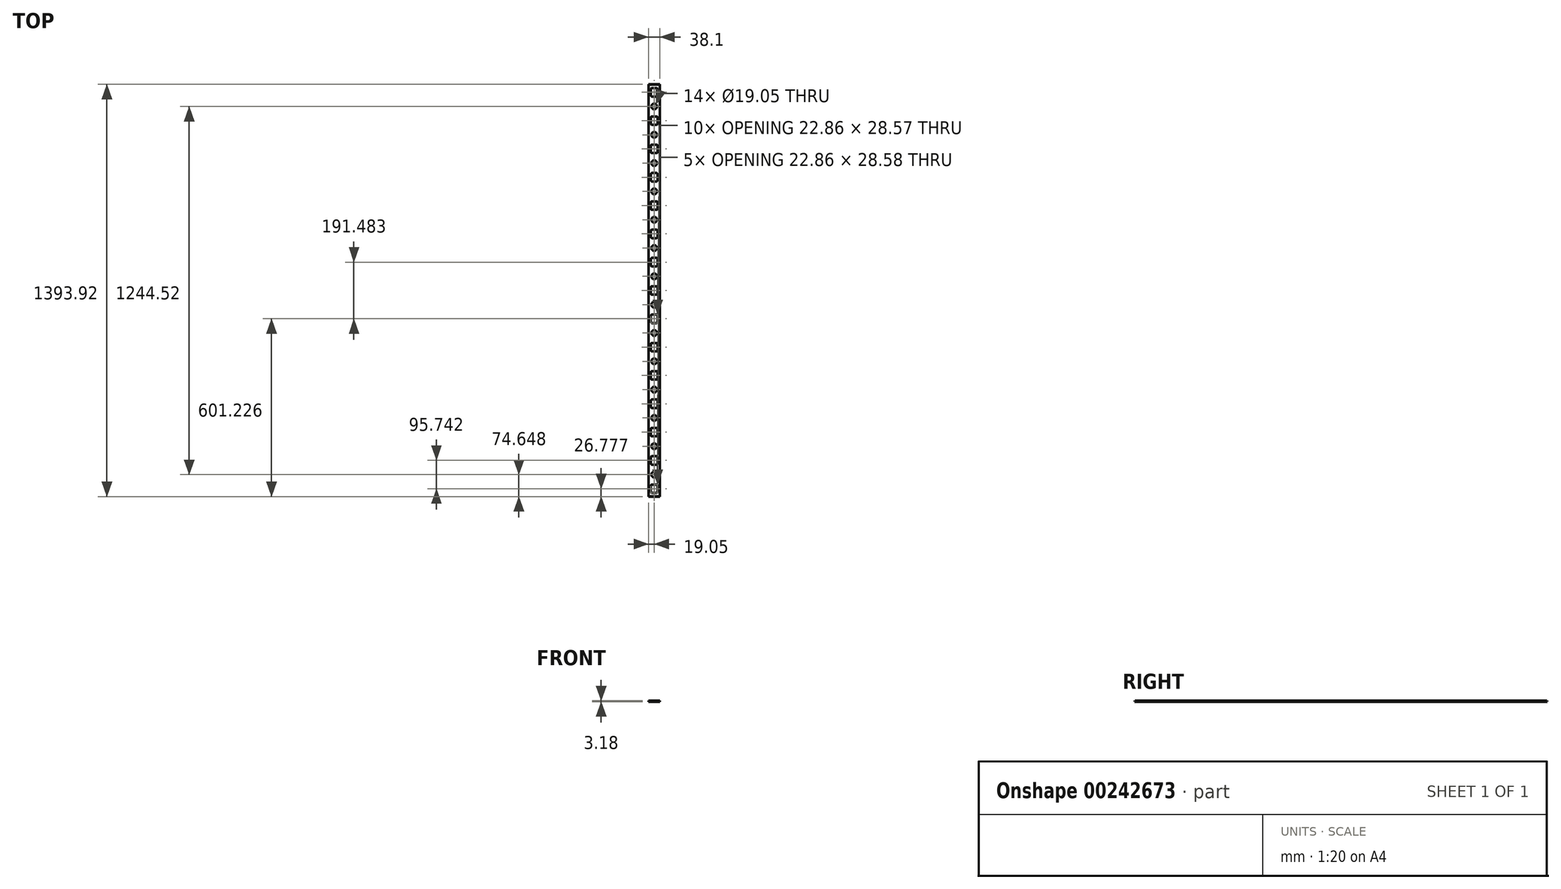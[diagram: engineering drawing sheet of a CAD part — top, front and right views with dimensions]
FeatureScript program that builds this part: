
annotation { "Feature Type Name" : "Feature", "Feature Type Description" : "" }
export const myFeature = defineFeature(function(context is Context, id is Id, definition is map)
    precondition{}
    {
        {
            var Q0;
            Q0=qCreatedBy(makeId("Front.planeOp"),FACE);
            var sketch = newSketch(context, id + "F0", { "sketchPlane" : qUnion([Q0])});
            skLineSegment(sketch, "E0.bottom", {"start": v(19.05, -1.59) * mm, "end": v(-19.05, -1.59) * mm});
            skLineSegment(sketch, "E0.top", {"start": v(19.05, 1.59) * mm, "end": v(-19.05, 1.59) * mm});
            skLineSegment(sketch, "E0.left", {"start": v(19.05, -1.59) * mm, "end": v(19.05, 1.59) * mm});
            skLineSegment(sketch, "E0.right", {"start": v(-19.05, -1.59) * mm, "end": v(-19.05, 1.59) * mm});
            skPoint(sketch, "E0.middle", {"position": v(0, 0) * mm});
            skSolve(sketch);
        }
        {
            var Q0;
            Q0 = qSketchRegion(id + "F0", true);
            extrude(context, id + "F1", {"entities" : qUnion([Q0]), "depth" : 696.96 * mm, "hasSecondDirection" : true, "secondDirectionOppositeDirection" : true, "secondDirectionDepth" : 696.96 * mm});
        }
        {
            var Q0;
            Q0=makeQuery(id+"F1.opExtrude","SWEPT_FACE",FACE,{"disambiguationData":[OSD([sQuery(id+"F0.wireOp",EDGE,"E0.left")])]});
            var sketch = newSketch(context, id + "F2", { "sketchPlane" : qUnion([Q0])});
            skLineSegment(sketch, "E1", {"start": v(-696.96, -1.59) * mm, "end": v(-696.96, 1.59) * mm});
            skLineSegment(sketch, "E2", {"start": v(-696.96, -1.59) * mm, "end": v(-695.58, 1.59) * mm});
            skLineSegment(sketch, "E3", {"start": v(-695.58, 1.59) * mm, "end": v(-696.96, 1.59) * mm});
            skLineSegment(sketch, "E4", {"start": v(0, 0) * mm, "end": v(0, -127.2) * mm, "construction": true});
            skLineSegment(sketch, "E5.MirrorCS", {"start": v(696.96, -1.59) * mm, "end": v(695.58, 1.59) * mm});
            skLineSegment(sketch, "E6.MirrorCS", {"start": v(696.96, -1.59) * mm, "end": v(696.96, 1.59) * mm});
            skLineSegment(sketch, "E7.MirrorCS", {"start": v(695.58, 1.59) * mm, "end": v(696.96, 1.59) * mm});
            skSolve(sketch);
        }
        {
            var Q0;
            Q0 = qSketchRegion(id + "F2", true);
            var Q1;
            Q1=makeQuery(id+"F1.opExtrude","SWEPT_FACE",FACE,{"disambiguationData":[OSD([sQuery(id+"F0.wireOp",EDGE,"E0.right")])]});
            extrude(context, id + "F3", {"entities" : qUnion([Q0]), "operationType" : NewBodyOperationType.REMOVE, "endBound" : BoundingType.UP_TO_SURFACE, "oppositeDirection" : true, "endBoundEntityFace" : qUnion([Q1]), "depth" : 25.4 * mm});
        }
        {
            var Q0;
            Q0=makeQuery(id+"F1.opExtrude","SWEPT_FACE",FACE,{"disambiguationData":[OSD([sQuery(id+"F0.wireOp",EDGE,"E0.top")])]});
            var sketch = newSketch(context, id + "F4", { "sketchPlane" : qUnion([Q0])});
            skLineSegment(sketch, "E8.bottom", {"start": v(7.62, -684.47) * mm, "end": v(-7.62, -684.47) * mm});
            skLineSegment(sketch, "E8.top", {"start": v(7.62, -655.9) * mm, "end": v(-7.62, -655.9) * mm});
            skLineSegment(sketch, "E8.left", {"start": v(11.43, -680.66) * mm, "end": v(11.43, -659.7) * mm});
            skLineSegment(sketch, "E8.right", {"start": v(-11.43, -680.66) * mm, "end": v(-11.43, -659.7) * mm});
            skPoint(sketch, "E8.middle", {"position": v(0, -670.18) * mm});
            skPoint(sketch, "E9.visualSharp", {"position": v(11.43, -655.9) * mm});
            skArc(sketch, "E9.filletArc", {"start": v(11.43, -659.7) * mm, "mid": v(10.31, -657.01) * mm, "end": v(7.62, -655.9) * mm});
            skPoint(sketch, "E10.visualSharp", {"position": v(-11.43, -655.9) * mm});
            skArc(sketch, "E10.filletArc", {"start": v(-7.62, -655.9) * mm, "mid": v(-10.31, -657.01) * mm, "end": v(-11.43, -659.7) * mm});
            skPoint(sketch, "E11.visualSharp", {"position": v(-11.43, -684.47) * mm});
            skArc(sketch, "E11.filletArc", {"start": v(-11.43, -680.66) * mm, "mid": v(-10.31, -683.35) * mm, "end": v(-7.62, -684.47) * mm});
            skPoint(sketch, "E12.visualSharp", {"position": v(11.43, -684.47) * mm});
            skArc(sketch, "E12.filletArc", {"start": v(7.62, -684.47) * mm, "mid": v(10.31, -683.35) * mm, "end": v(11.43, -680.66) * mm});
            skArc(sketch, "E13.0.1.0", {"start": v(7.62, -588.73) * mm, "mid": v(10.31, -587.61) * mm, "end": v(11.43, -584.92) * mm});
            skArc(sketch, "E13.0.1.1", {"start": v(11.43, -563.96) * mm, "mid": v(10.31, -561.27) * mm, "end": v(7.62, -560.15) * mm});
            skLineSegment(sketch, "E13.0.1.2", {"start": v(7.62, -560.15) * mm, "end": v(-7.62, -560.15) * mm});
            skLineSegment(sketch, "E13.0.1.3", {"start": v(-11.43, -584.92) * mm, "end": v(-11.43, -563.96) * mm});
            skArc(sketch, "E13.0.1.4", {"start": v(-11.43, -584.92) * mm, "mid": v(-10.31, -587.61) * mm, "end": v(-7.62, -588.73) * mm});
            skLineSegment(sketch, "E13.0.1.5", {"start": v(7.62, -588.73) * mm, "end": v(-7.62, -588.73) * mm});
            skLineSegment(sketch, "E13.0.1.6", {"start": v(11.43, -584.92) * mm, "end": v(11.43, -563.96) * mm});
            skArc(sketch, "E13.0.1.7", {"start": v(-7.62, -560.15) * mm, "mid": v(-10.31, -561.27) * mm, "end": v(-11.43, -563.96) * mm});
            skArc(sketch, "E13.0.2.0", {"start": v(7.62, -492.99) * mm, "mid": v(10.31, -491.87) * mm, "end": v(11.43, -489.18) * mm});
            skArc(sketch, "E13.0.2.1", {"start": v(11.43, -468.22) * mm, "mid": v(10.31, -465.53) * mm, "end": v(7.62, -464.41) * mm});
            skLineSegment(sketch, "E13.0.2.2", {"start": v(7.62, -464.41) * mm, "end": v(-7.62, -464.41) * mm});
            skLineSegment(sketch, "E13.0.2.3", {"start": v(-11.43, -489.18) * mm, "end": v(-11.43, -468.22) * mm});
            skArc(sketch, "E13.0.2.4", {"start": v(-11.43, -489.18) * mm, "mid": v(-10.31, -491.87) * mm, "end": v(-7.62, -492.99) * mm});
            skLineSegment(sketch, "E13.0.2.5", {"start": v(7.62, -492.99) * mm, "end": v(-7.62, -492.99) * mm});
            skLineSegment(sketch, "E13.0.2.6", {"start": v(11.43, -489.18) * mm, "end": v(11.43, -468.22) * mm});
            skArc(sketch, "E13.0.2.7", {"start": v(-7.62, -464.41) * mm, "mid": v(-10.31, -465.53) * mm, "end": v(-11.43, -468.22) * mm});
            skArc(sketch, "E13.0.3.0", {"start": v(7.62, -397.25) * mm, "mid": v(10.31, -396.13) * mm, "end": v(11.43, -393.44) * mm});
            skArc(sketch, "E13.0.3.1", {"start": v(11.43, -372.48) * mm, "mid": v(10.31, -369.79) * mm, "end": v(7.62, -368.67) * mm});
            skLineSegment(sketch, "E13.0.3.2", {"start": v(7.62, -368.67) * mm, "end": v(-7.62, -368.67) * mm});
            skLineSegment(sketch, "E13.0.3.3", {"start": v(-11.43, -393.44) * mm, "end": v(-11.43, -372.48) * mm});
            skArc(sketch, "E13.0.3.4", {"start": v(-11.43, -393.44) * mm, "mid": v(-10.31, -396.13) * mm, "end": v(-7.62, -397.25) * mm});
            skLineSegment(sketch, "E13.0.3.5", {"start": v(7.62, -397.25) * mm, "end": v(-7.62, -397.25) * mm});
            skLineSegment(sketch, "E13.0.3.6", {"start": v(11.43, -393.44) * mm, "end": v(11.43, -372.48) * mm});
            skArc(sketch, "E13.0.3.7", {"start": v(-7.62, -368.67) * mm, "mid": v(-10.31, -369.79) * mm, "end": v(-11.43, -372.48) * mm});
            skArc(sketch, "E13.0.4.0", {"start": v(7.62, -301.5) * mm, "mid": v(10.31, -300.39) * mm, "end": v(11.43, -297.7) * mm});
            skArc(sketch, "E13.0.4.1", {"start": v(11.43, -276.74) * mm, "mid": v(10.31, -274.05) * mm, "end": v(7.62, -272.93) * mm});
            skLineSegment(sketch, "E13.0.4.2", {"start": v(7.62, -272.93) * mm, "end": v(-7.62, -272.93) * mm});
            skLineSegment(sketch, "E13.0.4.3", {"start": v(-11.43, -297.7) * mm, "end": v(-11.43, -276.74) * mm});
            skArc(sketch, "E13.0.4.4", {"start": v(-11.43, -297.7) * mm, "mid": v(-10.31, -300.39) * mm, "end": v(-7.62, -301.5) * mm});
            skLineSegment(sketch, "E13.0.4.5", {"start": v(7.62, -301.5) * mm, "end": v(-7.62, -301.5) * mm});
            skLineSegment(sketch, "E13.0.4.6", {"start": v(11.43, -297.7) * mm, "end": v(11.43, -276.74) * mm});
            skArc(sketch, "E13.0.4.7", {"start": v(-7.62, -272.93) * mm, "mid": v(-10.31, -274.05) * mm, "end": v(-11.43, -276.74) * mm});
            skArc(sketch, "E13.0.5.0", {"start": v(7.62, -205.76) * mm, "mid": v(10.31, -204.65) * mm, "end": v(11.43, -201.95) * mm});
            skArc(sketch, "E13.0.5.1", {"start": v(11.43, -181) * mm, "mid": v(10.31, -178.3) * mm, "end": v(7.62, -177.19) * mm});
            skLineSegment(sketch, "E13.0.5.2", {"start": v(7.62, -177.19) * mm, "end": v(-7.62, -177.19) * mm});
            skLineSegment(sketch, "E13.0.5.3", {"start": v(-11.43, -201.95) * mm, "end": v(-11.43, -181) * mm});
            skArc(sketch, "E13.0.5.4", {"start": v(-11.43, -201.95) * mm, "mid": v(-10.31, -204.65) * mm, "end": v(-7.62, -205.76) * mm});
            skLineSegment(sketch, "E13.0.5.5", {"start": v(7.62, -205.76) * mm, "end": v(-7.62, -205.76) * mm});
            skLineSegment(sketch, "E13.0.5.6", {"start": v(11.43, -201.95) * mm, "end": v(11.43, -181) * mm});
            skArc(sketch, "E13.0.5.7", {"start": v(-7.62, -177.19) * mm, "mid": v(-10.31, -178.3) * mm, "end": v(-11.43, -181) * mm});
            skArc(sketch, "E13.0.6.0", {"start": v(7.62, -110.02) * mm, "mid": v(10.31, -108.9) * mm, "end": v(11.43, -106.21) * mm});
            skArc(sketch, "E13.0.6.1", {"start": v(11.43, -85.26) * mm, "mid": v(10.31, -82.56) * mm, "end": v(7.62, -81.45) * mm});
            skLineSegment(sketch, "E13.0.6.2", {"start": v(7.62, -81.45) * mm, "end": v(-7.62, -81.45) * mm});
            skLineSegment(sketch, "E13.0.6.3", {"start": v(-11.43, -106.21) * mm, "end": v(-11.43, -85.26) * mm});
            skArc(sketch, "E13.0.6.4", {"start": v(-11.43, -106.21) * mm, "mid": v(-10.31, -108.9) * mm, "end": v(-7.62, -110.02) * mm});
            skLineSegment(sketch, "E13.0.6.5", {"start": v(7.62, -110.02) * mm, "end": v(-7.62, -110.02) * mm});
            skLineSegment(sketch, "E13.0.6.6", {"start": v(11.43, -106.21) * mm, "end": v(11.43, -85.26) * mm});
            skArc(sketch, "E13.0.6.7", {"start": v(-7.62, -81.45) * mm, "mid": v(-10.31, -82.56) * mm, "end": v(-11.43, -85.26) * mm});
            skArc(sketch, "E13.0.7.0", {"start": v(7.62, -14.28) * mm, "mid": v(10.31, -13.16) * mm, "end": v(11.43, -10.47) * mm});
            skArc(sketch, "E13.0.7.1", {"start": v(11.43, 10.49) * mm, "mid": v(10.31, 13.18) * mm, "end": v(7.62, 14.3) * mm});
            skLineSegment(sketch, "E13.0.7.2", {"start": v(7.62, 14.3) * mm, "end": v(-7.62, 14.3) * mm});
            skLineSegment(sketch, "E13.0.7.3", {"start": v(-11.43, -10.47) * mm, "end": v(-11.43, 10.49) * mm});
            skArc(sketch, "E13.0.7.4", {"start": v(-11.43, -10.47) * mm, "mid": v(-10.31, -13.16) * mm, "end": v(-7.62, -14.28) * mm});
            skLineSegment(sketch, "E13.0.7.5", {"start": v(7.62, -14.28) * mm, "end": v(-7.62, -14.28) * mm});
            skLineSegment(sketch, "E13.0.7.6", {"start": v(11.43, -10.47) * mm, "end": v(11.43, 10.49) * mm});
            skArc(sketch, "E13.0.7.7", {"start": v(-7.62, 14.3) * mm, "mid": v(-10.31, 13.18) * mm, "end": v(-11.43, 10.49) * mm});
            skArc(sketch, "E13.0.8.0", {"start": v(7.62, 81.46) * mm, "mid": v(10.31, 82.58) * mm, "end": v(11.43, 85.27) * mm});
            skArc(sketch, "E13.0.8.1", {"start": v(11.43, 106.23) * mm, "mid": v(10.31, 108.92) * mm, "end": v(7.62, 110.04) * mm});
            skLineSegment(sketch, "E13.0.8.2", {"start": v(7.62, 110.04) * mm, "end": v(-7.62, 110.04) * mm});
            skLineSegment(sketch, "E13.0.8.3", {"start": v(-11.43, 85.27) * mm, "end": v(-11.43, 106.23) * mm});
            skArc(sketch, "E13.0.8.4", {"start": v(-11.43, 85.27) * mm, "mid": v(-10.31, 82.58) * mm, "end": v(-7.62, 81.46) * mm});
            skLineSegment(sketch, "E13.0.8.5", {"start": v(7.62, 81.46) * mm, "end": v(-7.62, 81.46) * mm});
            skLineSegment(sketch, "E13.0.8.6", {"start": v(11.43, 85.27) * mm, "end": v(11.43, 106.23) * mm});
            skArc(sketch, "E13.0.8.7", {"start": v(-7.62, 110.04) * mm, "mid": v(-10.31, 108.92) * mm, "end": v(-11.43, 106.23) * mm});
            skArc(sketch, "E13.0.9.0", {"start": v(7.62, 177.2) * mm, "mid": v(10.31, 178.32) * mm, "end": v(11.43, 181.01) * mm});
            skArc(sketch, "E13.0.9.1", {"start": v(11.43, 201.97) * mm, "mid": v(10.31, 204.66) * mm, "end": v(7.62, 205.78) * mm});
            skLineSegment(sketch, "E13.0.9.2", {"start": v(7.62, 205.78) * mm, "end": v(-7.62, 205.78) * mm});
            skLineSegment(sketch, "E13.0.9.3", {"start": v(-11.43, 181.01) * mm, "end": v(-11.43, 201.97) * mm});
            skArc(sketch, "E13.0.9.4", {"start": v(-11.43, 181.01) * mm, "mid": v(-10.31, 178.32) * mm, "end": v(-7.62, 177.2) * mm});
            skLineSegment(sketch, "E13.0.9.5", {"start": v(7.62, 177.2) * mm, "end": v(-7.62, 177.2) * mm});
            skLineSegment(sketch, "E13.0.9.6", {"start": v(11.43, 181.01) * mm, "end": v(11.43, 201.97) * mm});
            skArc(sketch, "E13.0.9.7", {"start": v(-7.62, 205.78) * mm, "mid": v(-10.31, 204.66) * mm, "end": v(-11.43, 201.97) * mm});
            skArc(sketch, "E13.0.10.0", {"start": v(7.62, 272.94) * mm, "mid": v(10.31, 274.06) * mm, "end": v(11.43, 276.75) * mm});
            skArc(sketch, "E13.0.10.1", {"start": v(11.43, 297.7) * mm, "mid": v(10.31, 300.4) * mm, "end": v(7.62, 301.52) * mm});
            skLineSegment(sketch, "E13.0.10.2", {"start": v(7.62, 301.52) * mm, "end": v(-7.62, 301.52) * mm});
            skLineSegment(sketch, "E13.0.10.3", {"start": v(-11.43, 276.75) * mm, "end": v(-11.43, 297.7) * mm});
            skArc(sketch, "E13.0.10.4", {"start": v(-11.43, 276.75) * mm, "mid": v(-10.31, 274.06) * mm, "end": v(-7.62, 272.94) * mm});
            skLineSegment(sketch, "E13.0.10.5", {"start": v(7.62, 272.94) * mm, "end": v(-7.62, 272.94) * mm});
            skLineSegment(sketch, "E13.0.10.6", {"start": v(11.43, 276.75) * mm, "end": v(11.43, 297.7) * mm});
            skArc(sketch, "E13.0.10.7", {"start": v(-7.62, 301.52) * mm, "mid": v(-10.31, 300.4) * mm, "end": v(-11.43, 297.7) * mm});
            skArc(sketch, "E13.0.11.0", {"start": v(7.62, 368.69) * mm, "mid": v(10.31, 369.8) * mm, "end": v(11.43, 372.5) * mm});
            skArc(sketch, "E13.0.11.1", {"start": v(11.43, 393.45) * mm, "mid": v(10.31, 396.15) * mm, "end": v(7.62, 397.26) * mm});
            skLineSegment(sketch, "E13.0.11.2", {"start": v(7.62, 397.26) * mm, "end": v(-7.62, 397.26) * mm});
            skLineSegment(sketch, "E13.0.11.3", {"start": v(-11.43, 372.5) * mm, "end": v(-11.43, 393.45) * mm});
            skArc(sketch, "E13.0.11.4", {"start": v(-11.43, 372.5) * mm, "mid": v(-10.31, 369.8) * mm, "end": v(-7.62, 368.69) * mm});
            skLineSegment(sketch, "E13.0.11.5", {"start": v(7.62, 368.69) * mm, "end": v(-7.62, 368.69) * mm});
            skLineSegment(sketch, "E13.0.11.6", {"start": v(11.43, 372.5) * mm, "end": v(11.43, 393.45) * mm});
            skArc(sketch, "E13.0.11.7", {"start": v(-7.62, 397.26) * mm, "mid": v(-10.31, 396.15) * mm, "end": v(-11.43, 393.45) * mm});
            skArc(sketch, "E13.0.12.0", {"start": v(7.62, 464.43) * mm, "mid": v(10.31, 465.54) * mm, "end": v(11.43, 468.24) * mm});
            skArc(sketch, "E13.0.12.1", {"start": v(11.43, 489.2) * mm, "mid": v(10.31, 491.89) * mm, "end": v(7.62, 493) * mm});
            skLineSegment(sketch, "E13.0.12.2", {"start": v(7.62, 493) * mm, "end": v(-7.62, 493) * mm});
            skLineSegment(sketch, "E13.0.12.3", {"start": v(-11.43, 468.24) * mm, "end": v(-11.43, 489.2) * mm});
            skArc(sketch, "E13.0.12.4", {"start": v(-11.43, 468.24) * mm, "mid": v(-10.31, 465.54) * mm, "end": v(-7.62, 464.43) * mm});
            skLineSegment(sketch, "E13.0.12.5", {"start": v(7.62, 464.43) * mm, "end": v(-7.62, 464.43) * mm});
            skLineSegment(sketch, "E13.0.12.6", {"start": v(11.43, 468.24) * mm, "end": v(11.43, 489.2) * mm});
            skArc(sketch, "E13.0.12.7", {"start": v(-7.62, 493) * mm, "mid": v(-10.31, 491.89) * mm, "end": v(-11.43, 489.2) * mm});
            skArc(sketch, "E13.0.13.0", {"start": v(7.62, 560.17) * mm, "mid": v(10.31, 561.28) * mm, "end": v(11.43, 563.98) * mm});
            skArc(sketch, "E13.0.13.1", {"start": v(11.43, 584.93) * mm, "mid": v(10.31, 587.63) * mm, "end": v(7.62, 588.74) * mm});
            skLineSegment(sketch, "E13.0.13.2", {"start": v(7.62, 588.74) * mm, "end": v(-7.62, 588.74) * mm});
            skLineSegment(sketch, "E13.0.13.3", {"start": v(-11.43, 563.98) * mm, "end": v(-11.43, 584.93) * mm});
            skArc(sketch, "E13.0.13.4", {"start": v(-11.43, 563.98) * mm, "mid": v(-10.31, 561.28) * mm, "end": v(-7.62, 560.17) * mm});
            skLineSegment(sketch, "E13.0.13.5", {"start": v(7.62, 560.17) * mm, "end": v(-7.62, 560.17) * mm});
            skLineSegment(sketch, "E13.0.13.6", {"start": v(11.43, 563.98) * mm, "end": v(11.43, 584.93) * mm});
            skArc(sketch, "E13.0.13.7", {"start": v(-7.62, 588.74) * mm, "mid": v(-10.31, 587.63) * mm, "end": v(-11.43, 584.93) * mm});
            skArc(sketch, "E13.0.14.0", {"start": v(7.62, 655.91) * mm, "mid": v(10.31, 657.03) * mm, "end": v(11.43, 659.72) * mm});
            skArc(sketch, "E13.0.14.1", {"start": v(11.43, 680.68) * mm, "mid": v(10.31, 683.37) * mm, "end": v(7.62, 684.49) * mm});
            skLineSegment(sketch, "E13.0.14.2", {"start": v(7.62, 684.49) * mm, "end": v(-7.62, 684.49) * mm});
            skLineSegment(sketch, "E13.0.14.3", {"start": v(-11.43, 659.72) * mm, "end": v(-11.43, 680.68) * mm});
            skArc(sketch, "E13.0.14.4", {"start": v(-11.43, 659.72) * mm, "mid": v(-10.31, 657.03) * mm, "end": v(-7.62, 655.91) * mm});
            skLineSegment(sketch, "E13.0.14.5", {"start": v(7.62, 655.91) * mm, "end": v(-7.62, 655.91) * mm});
            skLineSegment(sketch, "E13.0.14.6", {"start": v(11.43, 659.72) * mm, "end": v(11.43, 680.68) * mm});
            skArc(sketch, "E13.0.14.7", {"start": v(-7.62, 684.49) * mm, "mid": v(-10.31, 683.37) * mm, "end": v(-11.43, 680.68) * mm});
            skLineSegment(sketch, "E13.direction1", {"start": v(11.43, -680.66) * mm, "end": v(36.83, -680.66) * mm, "construction": true});
            skLineSegment(sketch, "E13.direction2", {"start": v(11.43, -680.66) * mm, "end": v(11.43, -584.92) * mm, "construction": true});
            skLineSegment(sketch, "E14", {"start": v(-11.43, -584.92) * mm, "end": v(-11.43, -659.7) * mm, "construction": true});
            skLineSegment(sketch, "E15", {"start": v(-11.43, -622.31) * mm, "end": v(11.43, -622.31) * mm, "construction": true});
            skCircle(sketch, "E16", {"center": v(0, -622.31) * mm, "radius": 9.53 * mm});
            skCircle(sketch, "E17.0.1.0", {"center": v(0, -526.58) * mm, "radius": 9.53 * mm});
            skCircle(sketch, "E17.0.2.0", {"center": v(0, -430.85) * mm, "radius": 9.53 * mm});
            skCircle(sketch, "E17.0.3.0", {"center": v(0, -335.11) * mm, "radius": 9.53 * mm});
            skCircle(sketch, "E17.0.4.0", {"center": v(0, -239.38) * mm, "radius": 9.53 * mm});
            skCircle(sketch, "E17.0.5.0", {"center": v(0, -143.65) * mm, "radius": 9.53 * mm});
            skCircle(sketch, "E17.0.6.0", {"center": v(0, -47.92) * mm, "radius": 9.53 * mm});
            skCircle(sketch, "E17.0.7.0", {"center": v(0, 47.82) * mm, "radius": 9.53 * mm});
            skCircle(sketch, "E17.0.8.0", {"center": v(0, 143.55) * mm, "radius": 9.53 * mm});
            skCircle(sketch, "E17.0.9.0", {"center": v(0, 239.28) * mm, "radius": 9.53 * mm});
            skCircle(sketch, "E17.0.10.0", {"center": v(0, 335.01) * mm, "radius": 9.53 * mm});
            skCircle(sketch, "E17.0.11.0", {"center": v(0, 430.75) * mm, "radius": 9.53 * mm});
            skCircle(sketch, "E17.0.12.0", {"center": v(0, 526.48) * mm, "radius": 9.53 * mm});
            skCircle(sketch, "E17.0.13.0", {"center": v(0, 622.21) * mm, "radius": 9.53 * mm});
            skLineSegment(sketch, "E17.direction1", {"start": v(0, -622.31) * mm, "end": v(25.4, -622.31) * mm, "construction": true});
            skLineSegment(sketch, "E17.direction2", {"start": v(0, -622.31) * mm, "end": v(0, -526.58) * mm, "construction": true});
            skSolve(sketch);
        }
        {
            var Q0;
            Q0 = qSketchRegion(id + "F4", true);
            var Q1;
            Q1=makeQuery(id+"F1.opExtrude","SWEPT_FACE",FACE,{"disambiguationData":[OSD([sQuery(id+"F0.wireOp",EDGE,"E0.bottom")])]});
            extrude(context, id + "F5", {"entities" : qUnion([Q0]), "operationType" : NewBodyOperationType.REMOVE, "endBound" : BoundingType.UP_TO_SURFACE, "oppositeDirection" : true, "endBoundEntityFace" : qUnion([Q1]), "depth" : 25.4 * mm});
        }
    });
